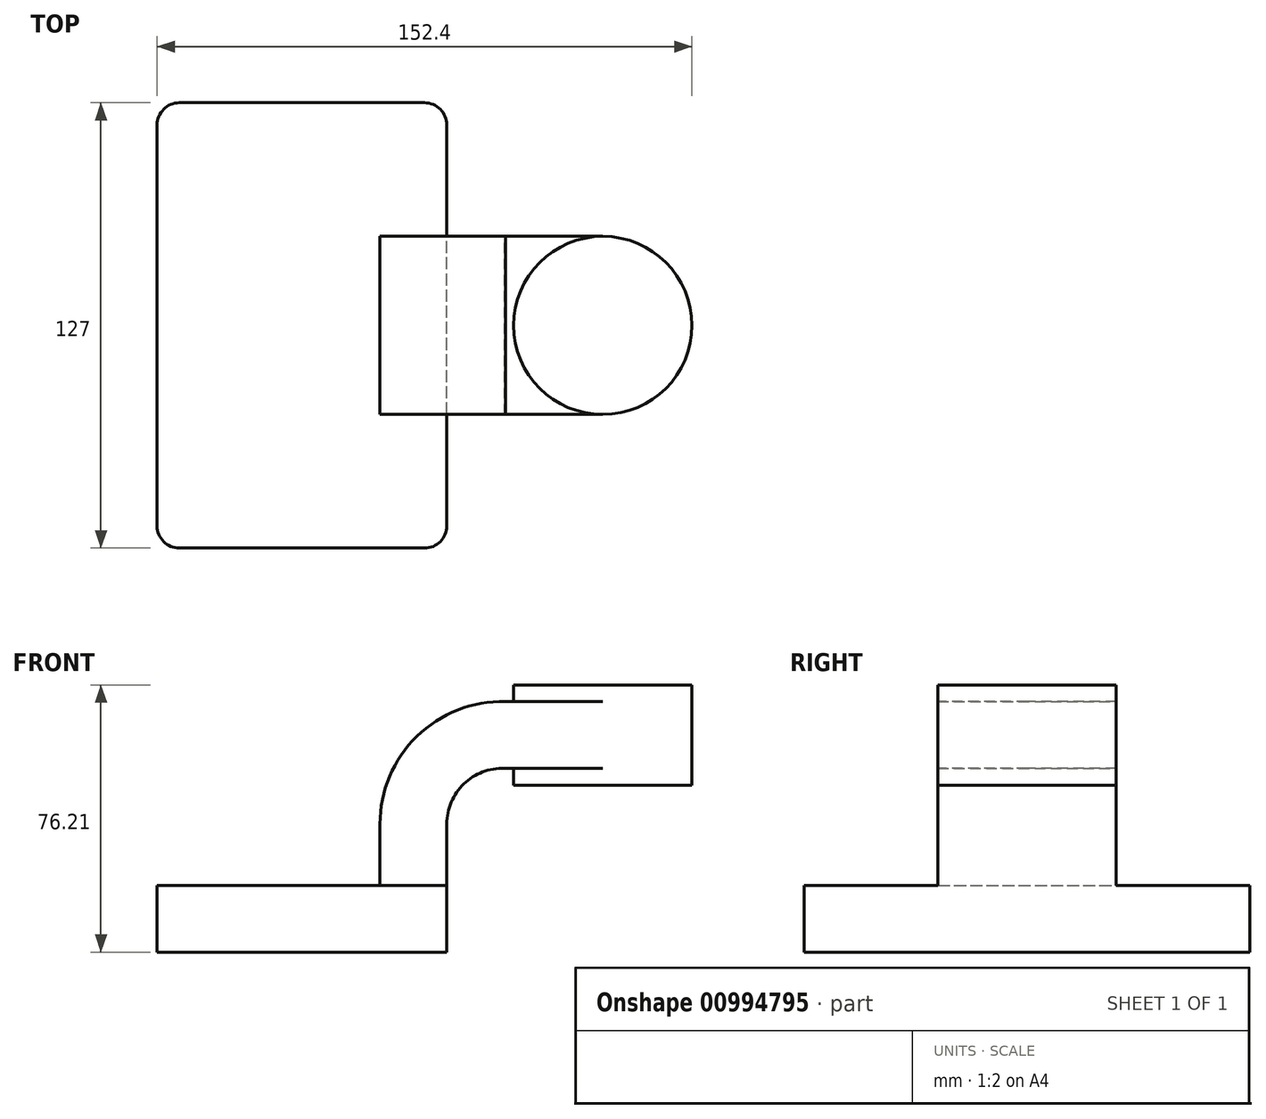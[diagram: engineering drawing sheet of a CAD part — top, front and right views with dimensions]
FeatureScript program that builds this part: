
annotation { "Feature Type Name" : "Feature", "Feature Type Description" : "" }
export const myFeature = defineFeature(function(context is Context, id is Id, definition is map)
    precondition{}
    {
        {
            var Q0;
            Q0=qCreatedBy(makeId("Front.planeOp"),FACE);
            var sketch = newSketch(context, id + "F0", { "sketchPlane" : qUnion([Q0])});
            skLineSegment(sketch, "E0.bottom", {"start": v(-41.28, -9.53) * mm, "end": v(41.28, -9.53) * mm});
            skLineSegment(sketch, "E0.top", {"start": v(-41.28, 9.53) * mm, "end": v(41.28, 9.53) * mm});
            skLineSegment(sketch, "E0.left", {"start": v(-41.28, -9.53) * mm, "end": v(-41.28, 9.53) * mm});
            skLineSegment(sketch, "E0.right", {"start": v(41.28, -9.53) * mm, "end": v(41.28, 9.53) * mm});
            skPoint(sketch, "E0.middle", {"position": v(0, 0) * mm});
            skLineSegment(sketch, "E1.bottom", {"start": v(60.33, 66.67) * mm, "end": v(111.12, 66.67) * mm});
            skLineSegment(sketch, "E1.top", {"start": v(60.32, 38.1) * mm, "end": v(111.12, 38.1) * mm});
            skLineSegment(sketch, "E1.left", {"start": v(60.33, 66.67) * mm, "end": v(60.32, 38.1) * mm});
            skLineSegment(sketch, "E1.right", {"start": v(111.13, 66.67) * mm, "end": v(111.12, 38.1) * mm});
            skLineSegment(sketch, "E2", {"start": v(41.28, 9.53) * mm, "end": v(41.28, 27.01) * mm});
            skArc(sketch, "E3", {"start": v(41.27, 27.01) * mm, "mid": v(46.13, 38.43) * mm, "end": v(57.71, 42.88) * mm});
            skLineSegment(sketch, "E4", {"start": v(57.71, 42.88) * mm, "end": v(85.72, 42.88) * mm});
            skPoint(sketch, "E4.endSnap0", {"position": v(85.72, 66.67) * mm});
            skLineSegment(sketch, "E5.0", {"start": v(57.99, 61.93) * mm, "end": v(85.72, 61.93) * mm});
            skArc(sketch, "E5.1", {"start": v(22.22, 27.01) * mm, "mid": v(32.75, 52) * mm, "end": v(57.99, 61.93) * mm});
            skLineSegment(sketch, "E5.2", {"start": v(22.22, 9.53) * mm, "end": v(22.22, 27.01) * mm});
            skFitSpline(sketch, "E6", {"points": [v(-41.28, 9.53) * mm, v(57.99, 61.93) * mm], "startDerivative": vector(57.5, 111.37) * mm, "endDerivative": vector(104.57, -9) * mm});
            skLineSegment(sketch, "E7", {"start": v(85.72, 38.1) * mm, "end": v(85.72, 66.67) * mm});
            skSolve(sketch);
        }
        {
            var Q0;
            Q0=makeQuery(id+"F0.imprint","IMPRINT",FACE,{"disambiguationData":[TD([[makeQuery(id+"F0.imprint","IMPRINT",EDGE,{"derivedFrom":sQuery(id+"F0.wireOp",EDGE,"E0.bottom")}),1.0]])]});
            extrude(context, id + "F1", {"entities" : qUnion([Q0]), "endBound" : BoundingType.SYMMETRIC, "depth" : 127 * mm, "offsetDistance" : 25.4 * mm});
        }
        {
            var Q0;
            {var subQ1=sQuery(id+"F0.wireOp",EDGE,"E2");Q0=makeQuery(id+"F0.imprint","IMPRINT",FACE,{"disambiguationData":[TD([[makeQuery(id+"F0.imprint","IMPRINT",EDGE,{"derivedFrom":subQ1}),1.0]])]});}
            var Q1;
            {var subQ0=sQuery(id+"F0.wireOp",EDGE,"E5.0");var subQ1=sQuery(id+"F0.wireOp",EDGE,"E1.left");var subQ2=makeQuery(id+"F0.imprint","INTERSECT",VERTEX,{"derivedFrom":[subQ1,subQ0]});Q1=makeQuery(id+"F0.imprint","IMPRINT",FACE,{"disambiguationData":[TD([[makeQuery(id+"F0.imprint","IMPRINT",EDGE,{"disambiguationData":[TD([[subQ2,-1.0]])],"derivedFrom":subQ1}),1.0]])]});}
            extrude(context, id + "F2", {"entities" : qUnion([Q0, Q1]), "operationType" : NewBodyOperationType.ADD, "endBound" : BoundingType.SYMMETRIC, "depth" : 50.8 * mm, "offsetDistance" : 25.4 * mm});
        }
        {
            var Q0;
            Q0=makeQuery(id+"F0.imprint","IMPRINT",FACE,{"disambiguationData":[TD([[makeQuery(id+"F0.imprint","IMPRINT",EDGE,{"derivedFrom":sQuery(id+"F0.wireOp",EDGE,"E5.1")}),1.0]])]});
            extrude(context, id + "F3", {"entities" : qUnion([Q0]), "operationType" : NewBodyOperationType.ADD, "endBound" : BoundingType.SYMMETRIC, "depth" : 15.88 * mm, "offsetDistance" : 25.4 * mm});
        }
        {
            var Q0;
            {var subQ4=sQuery(id+"F0.wireOp",EDGE,"E1.right");Q0=makeQuery(id+"F0.imprint","IMPRINT",FACE,{"disambiguationData":[TD([[makeQuery(id+"F0.imprint","IMPRINT",EDGE,{"derivedFrom":subQ4}),-1.0]])]});}
            var Q1;
            Q1=sQuery(id+"F0.wireOp",EDGE,"E7");
            revolve(context, id + "F4", {"operationType" : NewBodyOperationType.ADD, "surfaceOperationType" : NewSurfaceOperationType.NEW, "entities" : qUnion([Q0]), "axis" : qUnion([Q1]), "revolveType" : RevolveType.FULL});
        }
        {
            var Q0;
            Q0=makeQuery(id+"F1.opExtrude","CAP_EDGE",EDGE,{"disambiguationData":[OSD([sQuery(id+"F0.wireOp",EDGE,"E0.left")])],"isStart":false});
            var Q1;
            Q1=makeQuery(id+"F1.opExtrude","CAP_EDGE",EDGE,{"disambiguationData":[OSD([sQuery(id+"F0.wireOp",EDGE,"E0.right")])],"isStart":false});
            var Q2;
            Q2=makeQuery(id+"F1.opExtrude","CAP_EDGE",EDGE,{"disambiguationData":[OSD([sQuery(id+"F0.wireOp",EDGE,"E0.right")])],"isStart":true});
            var Q3;
            Q3=makeQuery(id+"F1.opExtrude","CAP_EDGE",EDGE,{"disambiguationData":[OSD([sQuery(id+"F0.wireOp",EDGE,"E0.left")])],"isStart":true});
            fillet(context, id + "F5", {"entities" : qUnion([Q0, Q1, Q2, Q3]), "radius" : 6.35 * mm, "tangentPropagation" : true, "allowEdgeOverflow" : false});
        }
    });
